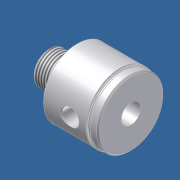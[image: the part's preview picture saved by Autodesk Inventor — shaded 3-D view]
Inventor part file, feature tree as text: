
AUTODESK INVENTOR PART (.ipt)
format: ipt  version: unknown  size: 312,320 bytes
history: native  units: in
note: dims shown in document units (in); Inventor stores cm internally (conversion verified against a paired STEP export)
features: other x112, revolve x5, sketch x5, thread x1
ambient origin geometry x8: Origin, YZ Plane, XZ Plane, XY Plane, X Axis, Y Axis, Z Axis, Center Point
feature tree (123):
  revolve  "Revolution1"  [1 undecoded]
  thread  "Thread1"  [1 undecoded]
  revolve  "Revolution2"  Angle=360.0deg
  revolve  "Revolution3"  [1 undecoded]
  revolve  "Revolution4"  [1 undecoded]
  revolve  "Revolution5"  [1 undecoded]
  other  "dp1_XY"
  other  "dp1_YZ"
  other  "dp1_ZX"
  other  "dp1_X"
  other  "dp1_Y"
  other  "dp1_Z"
  other  "dp1_Center"
  other  "dp2_XY"
  other  "dp2_YZ"
  other  "dp2_ZX"
  other  "dp2_X"
  other  "dp2_Y"
  other  "dp2_Z"
  other  "dp2_Center"
  other  "port_XY"
  other  "port_YZ"
  other  "port_ZX"
  other  "port_X"
  other  "port_Y"
  other  "port_Z"
  other  "port_Center"
  other  "rod_guide_XY"
  other  "rod_guide_YZ"
  other  "rod_guide_ZX"
  other  "rod_guide_X"
  other  "rod_guide_Y"
  other  "rod_guide_Z"
  other  "rod_guide_Center"
  other  "s1_XY"
  other  "s1_YZ"
  other  "s1_ZX"
  other  "s1_X"
  other  "s1_Y"
  other  "s1_Z"
  other  "s1_Center"
  other  "s2_XY"
  other  "s2_YZ"
  other  "s2_ZX"
  other  "s2_X"
  other  "s2_Y"
  other  "s2_Z"
  other  "s2_Center"
  other  "t1_XY"
  other  "t1_YZ"
  other  "t1_ZX"
  other  "t1_X"
  other  "t1_Y"
  other  "t1_Z"
  other  "t1_Center"
  other  "t111_XY"
  other  "t111_YZ"
  other  "t111_ZX"
  other  "t111_X"
  other  "t111_Y"
  other  "t111_Z"
  other  "t111_Center"
  other  "to_foot_bracket_XY"
  other  "to_foot_bracket_YZ"
  other  "to_foot_bracket_ZX"
  other  "to_foot_bracket_X"
  other  "to_foot_bracket_Y"
  other  "to_foot_bracket_Z"
  other  "to_foot_bracket_Center"
  other  "to_nut_XY"
  other  "to_nut_YZ"
  other  "to_nut_ZX"
  other  "to_nut_X"
  other  "to_nut_Y"
  other  "to_nut_Z"
  other  "to_nut_Center"
  other  "to_rod_XY"
  other  "to_rod_YZ"
  other  "to_rod_ZX"
  other  "to_rod_X"
  other  "to_rod_Y"
  other  "to_rod_Z"
  other  "to_rod_Center"
  other  "to_screw_XY"
  other  "to_screw_YZ"
  other  "to_screw_ZX"
  other  "to_screw_X"
  other  "to_screw_Y"
  other  "to_screw_Z"
  other  "to_screw_Center"
  other  "to_trunnion_brackets_XY"
  other  "to_trunnion_brackets_YZ"
  other  "to_trunnion_brackets_ZX"
  other  "to_trunnion_brackets_X"
  other  "to_trunnion_brackets_Y"
  other  "to_trunnion_brackets_Z"
  other  "to_trunnion_brackets_Center"
  other  "to_trunnion_brackets1_XY"
  other  "to_trunnion_brackets1_YZ"
  other  "to_trunnion_brackets1_ZX"
  other  "to_trunnion_brackets1_X"
  other  "to_trunnion_brackets1_Y"
  other  "to_trunnion_brackets1_Z"
  other  "to_trunnion_brackets1_Center"
  other  "to_trunnion_brackets2_XY"
  other  "to_trunnion_brackets2_YZ"
  other  "to_trunnion_brackets2_ZX"
  other  "to_trunnion_brackets2_X"
  other  "to_trunnion_brackets2_Y"
  other  "to_trunnion_brackets2_Z"
  other  "to_trunnion_brackets2_Center"
  other  "to_tube_XY"
  other  "to_tube_YZ"
  other  "to_tube_ZX"
  other  "to_tube_X"
  other  "to_tube_Y"
  other  "to_tube_Z"
  other  "to_tube_Center"
  sketch  "Sketch_2"  dims[d0=360.0deg d1=0.3995in d2=0.0in d3=360.0deg]
  sketch  "Sketch_3"  dims[d4=360.0deg d5=360.0deg]
  sketch  "Sketch_5"  dims[d6=360.0deg]
  sketch  "Sketch_40"
  sketch  "Sketch_47"
note: 5 required parameter values undecoded (feature->parameter linkage not recoverable at this tier; creation-order binding heuristic only, values carry confidence <= 0.55)